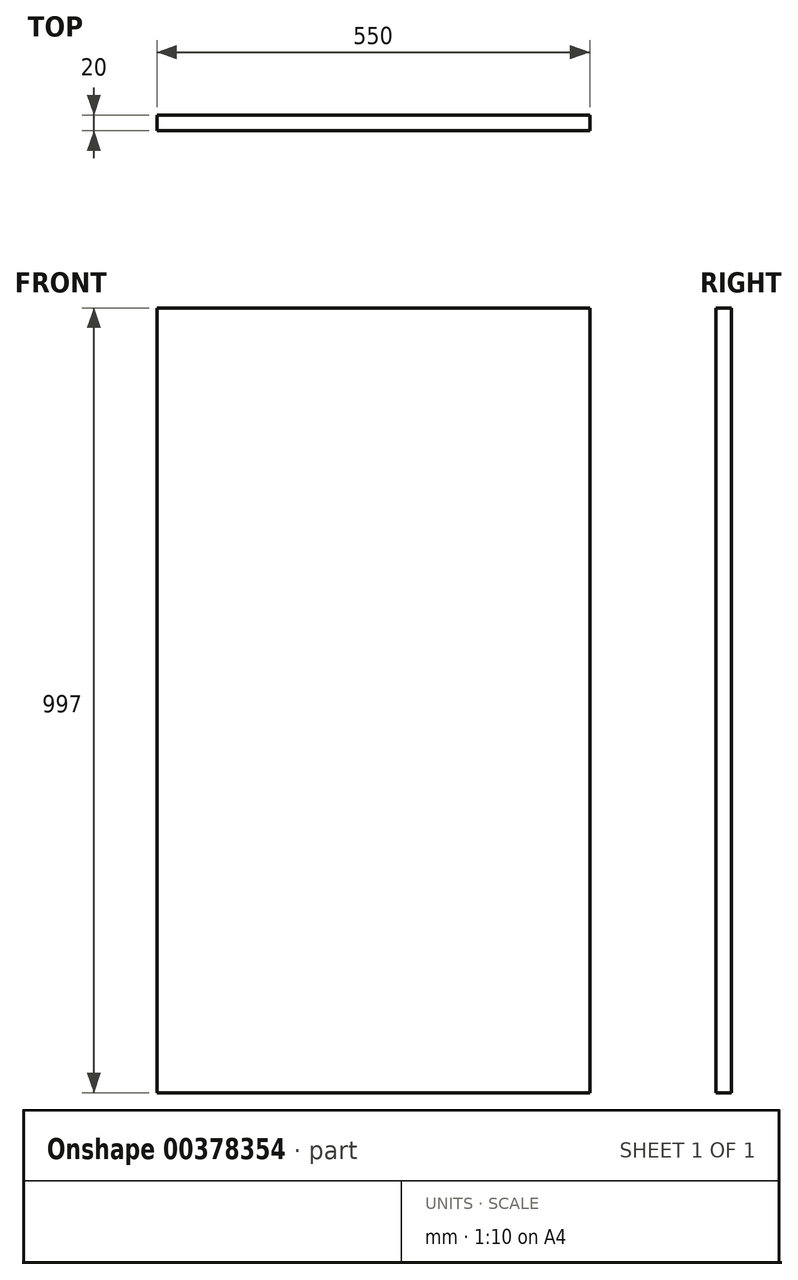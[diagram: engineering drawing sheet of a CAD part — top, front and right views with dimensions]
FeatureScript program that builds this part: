
annotation { "Feature Type Name" : "Feature", "Feature Type Description" : "" }
export const myFeature = defineFeature(function(context is Context, id is Id, definition is map)
    precondition{}
    {
        {
            var Q0;
            Q0=qCreatedBy(makeId("Front.planeOp"),FACE);
            var sketch = newSketch(context, id + "F0", { "sketchPlane" : qUnion([Q0])});
            skLineSegment(sketch, "E0.bottom", {"start": v(275, 498.5) * mm, "end": v(-275, 498.5) * mm});
            skLineSegment(sketch, "E0.top", {"start": v(275, -498.5) * mm, "end": v(-275, -498.5) * mm});
            skLineSegment(sketch, "E0.left", {"start": v(275, 498.5) * mm, "end": v(275, -498.5) * mm});
            skLineSegment(sketch, "E0.right", {"start": v(-275, 498.5) * mm, "end": v(-275, -498.5) * mm});
            skPoint(sketch, "E0.middle", {"position": v(0, 0) * mm});
            skSolve(sketch);
        }
        {
            var Q0;
            Q0 = qSketchRegion(id + "F0", true);
            extrude(context, id + "F1", {"entities" : qUnion([Q0]), "depth" : 20 * mm});
        }
    });
